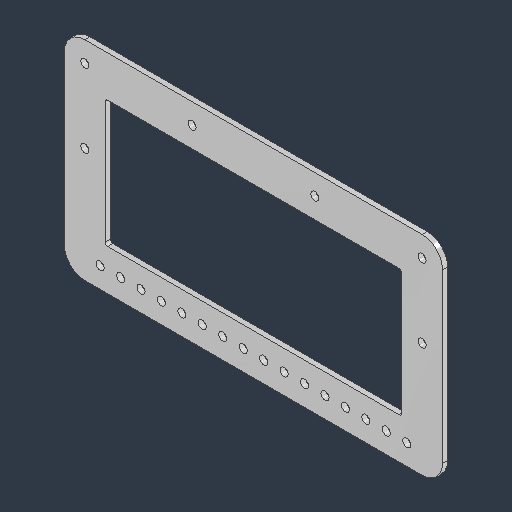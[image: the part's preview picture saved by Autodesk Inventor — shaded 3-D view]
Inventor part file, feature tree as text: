
AUTODESK INVENTOR PART (.ipt)
format: ipt  version: 2024.3 (Build 283343000, 343)  size: 170,496 bytes
history: native  units: in
note: dims shown in document units (in); Inventor stores cm internally (conversion verified against a paired STEP export)
features: chamfer x2, sketch x2, sheet_metal_op x1, hole x1, other x1
ambient origin geometry x8: Origin, YZ Plane, XZ Plane, XY Plane, X Axis, Y Axis, Z Axis, Center Point
bodies: Solid1 (feature_tree)
feature tree (7):
  sheet_metal_op  "Face1"
  hole  "Hole1"  [1 undecoded]
  chamfer  "Corner Round1"
  chamfer  "Corner Round2"
  sketch  "Sketch1"  dims[d0=7.25in d1=3.1in]
  other  "Plate1"
  sketch  "Sketch2"  dims[d2=1.0in d3=0.125in d4=0.5in d14=6.2992in d16=0.5in d17=0.3937in d19=1.0in d21=0.375in d22=0.375in d23=2.625in d24=2.625in d25=3.0in d26=1.8in d28=1.8in d29=0.201in d30=0.38in d31=0.385in d32=0.25in d33=0.5635in d34=0.125in d35=0.8108in d36=0.0625in d37=0.5in]
note: 1 required parameter value undecoded (feature->parameter linkage not recoverable at this tier; creation-order binding heuristic only, values carry confidence <= 0.55)
